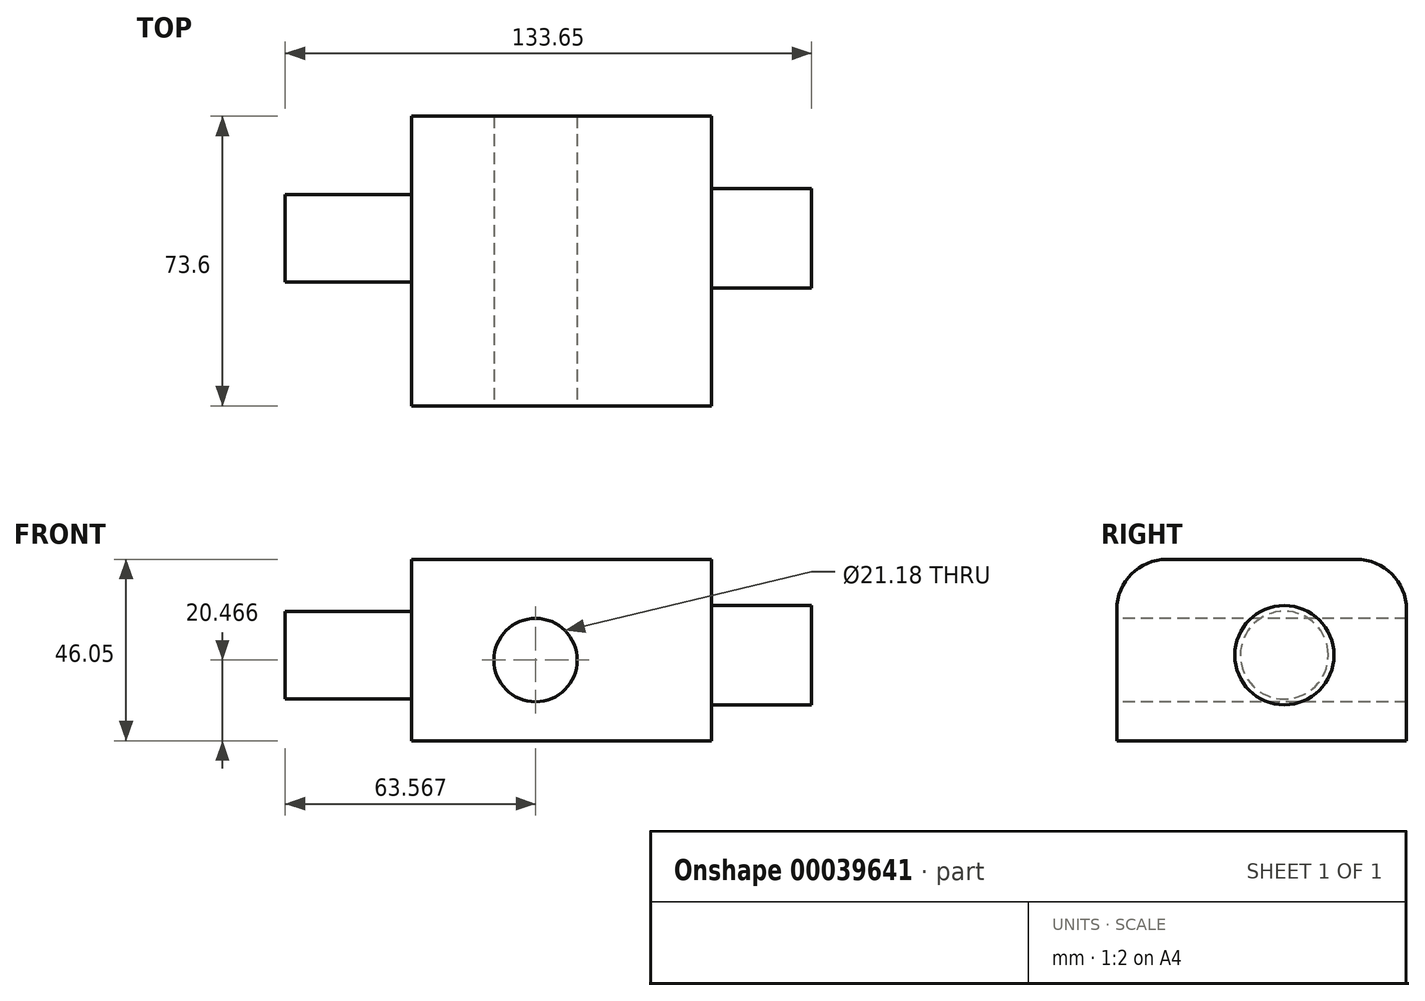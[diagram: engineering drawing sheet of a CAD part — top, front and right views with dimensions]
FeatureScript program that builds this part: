
annotation { "Feature Type Name" : "Feature", "Feature Type Description" : "" }
export const myFeature = defineFeature(function(context is Context, id is Id, definition is map)
    precondition{}
    {
        {
            var Q0;
            Q0=qCreatedBy(makeId("Right.planeOp"),FACE);
            var sketch = newSketch(context, id + "F0", { "sketchPlane" : qUnion([Q0])});
            skLineSegment(sketch, "E0.bottom", {"start": v(-42.58, 3.56) * mm, "end": v(31.02, 3.56) * mm});
            skLineSegment(sketch, "E0.top", {"start": v(-29.88, 49.61) * mm, "end": v(18.32, 49.61) * mm});
            skLineSegment(sketch, "E0.left", {"start": v(-42.58, 3.56) * mm, "end": v(-42.58, 36.91) * mm});
            skLineSegment(sketch, "E0.right", {"start": v(31.02, 3.56) * mm, "end": v(31.02, 36.91) * mm});
            skPoint(sketch, "E1.visualSharp", {"position": v(-42.58, 49.61) * mm});
            skArc(sketch, "E1.filletArc", {"start": v(-29.88, 49.61) * mm, "mid": v(-38.86, 45.9) * mm, "end": v(-42.58, 36.91) * mm});
            skPoint(sketch, "E2.visualSharp", {"position": v(31.02, 49.61) * mm});
            skArc(sketch, "E2.filletArc", {"start": v(31.02, 36.91) * mm, "mid": v(27.3, 45.9) * mm, "end": v(18.32, 49.61) * mm});
            skSolve(sketch);
        }
        {
            var Q0;
            Q0 = qSketchRegion(id + "F0", true);
            extrude(context, id + "F1", {"entities" : qUnion([Q0]), "depth" : 76.2 * mm});
        }
        {
            var Q0;
            Q0=makeQuery(id+"F1.opExtrude","CAP_FACE",FACE,{"disambiguationData":[OSD([sQuery(id+"F0.wireOp",EDGE,"E0.bottom"),sQuery(id+"F0.wireOp",EDGE,"E0.top"),sQuery(id+"F0.wireOp",EDGE,"E0.left"),sQuery(id+"F0.wireOp",EDGE,"E0.right"),sQuery(id+"F0.wireOp",EDGE,"E1.filletArc"),sQuery(id+"F0.wireOp",EDGE,"E2.filletArc")])],"isStart":false});
            var sketch = newSketch(context, id + "F2", { "sketchPlane" : qUnion([Q0])});
            skCircle(sketch, "E3", {"center": v(0, 25.28) * mm, "radius": 12.6 * mm});
            skSolve(sketch);
        }
        {
            var Q0;
            Q0 = qSketchRegion(id + "F2", true);
            extrude(context, id + "F3", {"entities" : qUnion([Q0]), "operationType" : NewBodyOperationType.ADD, "depth" : 25.4 * mm});
        }
        {
            var Q0;
            Q0=makeQuery(id+"F3.opExtrude","CAP_FACE",FACE,{"disambiguationData":[OSD([sQuery(id+"F2.wireOp",EDGE,"E3")])],"isStart":false});
            var sketch = newSketch(context, id + "F4", { "sketchPlane" : qUnion([Q0])});
            skCircle(sketch, "E4", {"center": v(0, 25.28) * mm, "radius": 11.16 * mm});
            skSolve(sketch);
        }
        {
            var Q0;
            Q0 = qSketchRegion(id + "F4", true);
            extrude(context, id + "F5", {"entities" : qUnion([Q0]), "operationType" : NewBodyOperationType.ADD, "endBound" : BoundingType.THROUGH_ALL, "oppositeDirection" : true, "depth" : 25.4 * mm});
        }
        {
            var Q0;
            Q0=makeQuery(id+"F1.opExtrude","SWEPT_FACE",FACE,{"disambiguationData":[OSD([sQuery(id+"F0.wireOp",EDGE,"E0.left")])]});
            var sketch = newSketch(context, id + "F6", { "sketchPlane" : qUnion([Q0])});
            skCircle(sketch, "E5", {"center": v(31.52, 24.03) * mm, "radius": 10.59 * mm});
            skSolve(sketch);
        }
        {
            var Q0;
            Q0 = qSketchRegion(id + "F6", true);
            extrude(context, id + "F7", {"entities" : qUnion([Q0]), "operationType" : NewBodyOperationType.REMOVE, "endBound" : BoundingType.THROUGH_ALL, "oppositeDirection" : true, "depth" : 25.4 * mm});
        }
    });
